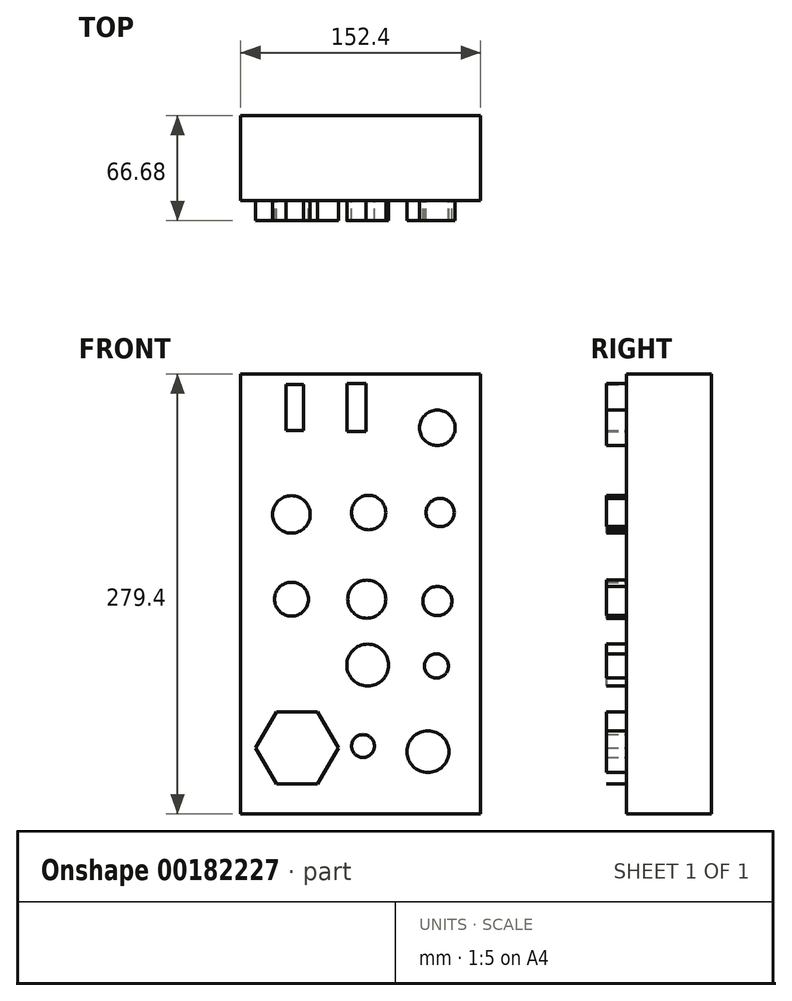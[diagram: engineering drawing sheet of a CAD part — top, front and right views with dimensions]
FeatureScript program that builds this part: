
annotation { "Feature Type Name" : "Feature", "Feature Type Description" : "" }
export const myFeature = defineFeature(function(context is Context, id is Id, definition is map)
    precondition{}
    {
        {
            var Q0;
            Q0=qCreatedBy(makeId("Front.planeOp"),FACE);
            var sketch = newSketch(context, id + "F0", { "sketchPlane" : qUnion([Q0])});
            skLineSegment(sketch, "E0.bottom", {"start": v(0, 0) * mm, "end": v(152.4, 0) * mm});
            skLineSegment(sketch, "E0.top", {"start": v(0, 279.4) * mm, "end": v(152.4, 279.4) * mm});
            skLineSegment(sketch, "E0.left", {"start": v(0, 0) * mm, "end": v(0, 279.4) * mm});
            skLineSegment(sketch, "E0.right", {"start": v(152.4, 0) * mm, "end": v(152.4, 279.4) * mm});
            skSolve(sketch);
        }
        {
            var Q0;
            Q0=makeQuery(id+"F0.imprint","IMPRINT",FACE,{"disambiguationData":[TD([[makeQuery(id+"F0.imprint","IMPRINT",EDGE,{"derivedFrom":sQuery(id+"F0.wireOp",EDGE,"E0.bottom")}),1.0]])]});
            extrude(context, id + "F1", {"entities" : qUnion([Q0]), "oppositeDirection" : true, "depth" : 53.97 * mm});
        }
        {
            var Q0;
            Q0=makeQuery(id+"F1.opExtrude","CAP_FACE",FACE,{"disambiguationData":[OSD([sQuery(id+"F0.wireOp",EDGE,"E0.bottom"),sQuery(id+"F0.wireOp",EDGE,"E0.top"),sQuery(id+"F0.wireOp",EDGE,"E0.left"),sQuery(id+"F0.wireOp",EDGE,"E0.right")])],"isStart":true});
            var sketch = newSketch(context, id + "F2", { "sketchPlane" : qUnion([Q0])});
            skPoint(sketch, "E1", {"position": v(32.25, 136.4) * mm});
            skPoint(sketch, "E2", {"position": v(32.25, 190.22) * mm});
            skPoint(sketch, "E3", {"position": v(81.28, 191.42) * mm});
            skPoint(sketch, "E4", {"position": v(80.09, 136.4) * mm});
            skPoint(sketch, "E5", {"position": v(80.68, 94.55) * mm});
            skPoint(sketch, "E6", {"position": v(77.7, 43.13) * mm});
            skPoint(sketch, "E7", {"position": v(126.73, 191.42) * mm});
            skPoint(sketch, "E8", {"position": v(124.93, 135.21) * mm});
            skPoint(sketch, "E9", {"position": v(124.34, 93.95) * mm});
            skPoint(sketch, "E10", {"position": v(118.95, 39.54) * mm});
            skPoint(sketch, "E11", {"position": v(35.84, 41.93) * mm});
            skPoint(sketch, "E12", {"position": v(124.93, 245.24) * mm});
            skPoint(sketch, "E13", {"position": v(79.49, 242.84) * mm});
            skPoint(sketch, "E14", {"position": v(28.66, 243.44) * mm});
            skCircle(sketch, "E15.cCircle", {"center": v(35.84, 41.93) * mm, "radius": 22.72 * mm, "construction": true});
            skLineSegment(sketch, "E15.0", {"start": v(22.72, 64.65) * mm, "end": v(48.96, 64.65) * mm});
            skLineSegment(sketch, "E15.1", {"start": v(48.96, 64.65) * mm, "end": v(62.08, 41.93) * mm});
            skLineSegment(sketch, "E15.2", {"start": v(62.08, 41.93) * mm, "end": v(48.96, 19.2) * mm});
            skLineSegment(sketch, "E15.3", {"start": v(48.96, 19.2) * mm, "end": v(22.72, 19.2) * mm});
            skLineSegment(sketch, "E15.4", {"start": v(22.72, 19.2) * mm, "end": v(9.6, 41.93) * mm});
            skLineSegment(sketch, "E15.5", {"start": v(9.6, 41.93) * mm, "end": v(22.72, 64.65) * mm});
            skPoint(sketch, "E15.0.midPoint", {"position": v(35.84, 64.65) * mm});
            skCircle(sketch, "E16", {"center": v(32.25, 136.4) * mm, "radius": 10.78 * mm});
            skCircle(sketch, "E17", {"center": v(32.25, 190.22) * mm, "radius": 11.91 * mm});
            skLineSegment(sketch, "E18.bottom", {"start": v(28.66, 243.44) * mm, "end": v(40.02, 243.44) * mm});
            skLineSegment(sketch, "E18.top", {"start": v(28.66, 272.74) * mm, "end": v(40.02, 272.74) * mm});
            skLineSegment(sketch, "E18.left", {"start": v(28.66, 243.44) * mm, "end": v(28.66, 272.74) * mm});
            skLineSegment(sketch, "E18.right", {"start": v(40.02, 243.44) * mm, "end": v(40.02, 272.74) * mm});
            skLineSegment(sketch, "E19.bottom", {"start": v(79.49, 242.84) * mm, "end": v(67.53, 242.84) * mm});
            skLineSegment(sketch, "E19.top", {"start": v(79.49, 273.34) * mm, "end": v(67.53, 273.34) * mm});
            skLineSegment(sketch, "E19.left", {"start": v(79.49, 242.84) * mm, "end": v(79.49, 273.34) * mm});
            skLineSegment(sketch, "E19.right", {"start": v(67.53, 242.84) * mm, "end": v(67.53, 273.34) * mm});
            skCircle(sketch, "E20", {"center": v(81.28, 191.42) * mm, "radius": 10.91 * mm});
            skCircle(sketch, "E21", {"center": v(80.09, 136.4) * mm, "radius": 12.1 * mm});
            skCircle(sketch, "E22", {"center": v(80.68, 94.55) * mm, "radius": 13.28 * mm});
            skCircle(sketch, "E23", {"center": v(118.95, 39.54) * mm, "radius": 13.28 * mm});
            skCircle(sketch, "E24", {"center": v(77.7, 43.13) * mm, "radius": 7.23 * mm});
            skCircle(sketch, "E25", {"center": v(124.34, 93.95) * mm, "radius": 7.66 * mm});
            skCircle(sketch, "E26", {"center": v(124.93, 135.21) * mm, "radius": 9.28 * mm});
            skCircle(sketch, "E27", {"center": v(126.73, 191.42) * mm, "radius": 8.97 * mm});
            skCircle(sketch, "E28", {"center": v(124.93, 245.24) * mm, "radius": 11.28 * mm});
            skSolve(sketch);
        }
        {
            var Q0;
            Q0=qSketchRegion(id+"F2",true);
            extrude(context, id + "F3", {"entities" : qUnion([Q0]), "operationType" : NewBodyOperationType.ADD, "depth" : 12.7 * mm});
        }
    });
